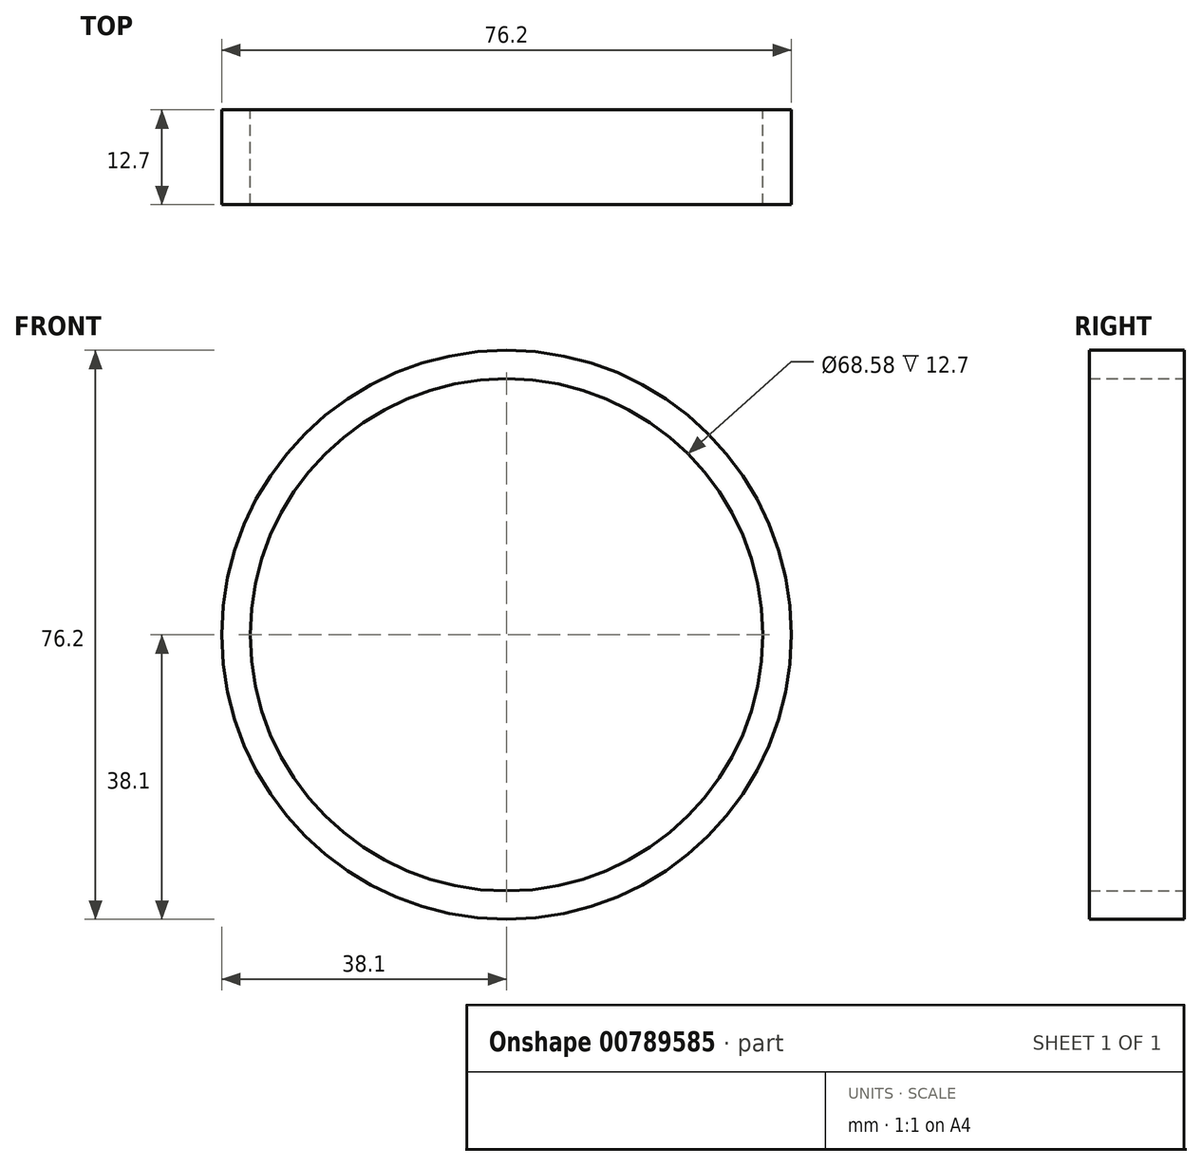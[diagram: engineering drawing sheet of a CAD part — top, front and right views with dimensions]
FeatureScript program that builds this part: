
annotation { "Feature Type Name" : "Feature", "Feature Type Description" : "" }
export const myFeature = defineFeature(function(context is Context, id is Id, definition is map)
    precondition{}
    {
        {
            var Q0;
            Q0=qCreatedBy(makeId("Front.planeOp"),FACE);
            var sketch = newSketch(context, id + "F0", { "sketchPlane" : qUnion([Q0])});
            skCircle(sketch, "E0", {"center": v(0, 0) * mm, "radius": 38.1 * mm});
            skCircle(sketch, "E1", {"center": v(0, 0) * mm, "radius": 34.3 * mm});
            skSolve(sketch);
        }
        {
            var Q0;
            Q0=makeQuery(id+"F0.imprint","IMPRINT",FACE,{"disambiguationData":[TD([[makeQuery(id+"F0.imprint","IMPRINT",EDGE,{"derivedFrom":sQuery(id+"F0.wireOp",EDGE,"E0")}),1.0]])]});
            extrude(context, id + "F1", {"entities" : qUnion([Q0]), "depth" : 12.7 * mm, "offsetDistance" : 25.4 * mm});
        }
    });
